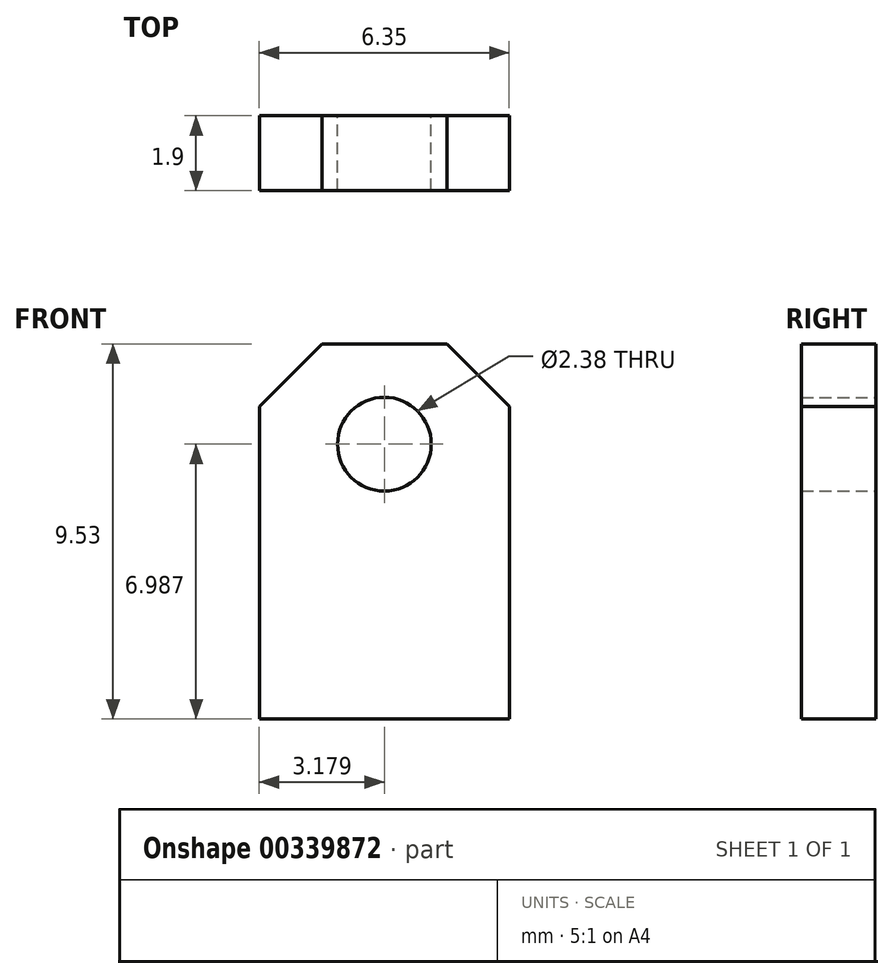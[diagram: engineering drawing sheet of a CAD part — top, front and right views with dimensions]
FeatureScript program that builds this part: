
annotation { "Feature Type Name" : "Feature", "Feature Type Description" : "" }
export const myFeature = defineFeature(function(context is Context, id is Id, definition is map)
    precondition{}
    {
        {
            var Q0;
            Q0=qCreatedBy(makeId("Front.planeOp"),FACE);
            var sketch = newSketch(context, id + "F0", { "sketchPlane" : qUnion([Q0])});
            skLineSegment(sketch, "E0.bottom", {"start": v(-34.55, 25.52) * mm, "end": v(-31.37, 25.52) * mm});
            skLineSegment(sketch, "E0.top", {"start": v(-36.14, 16) * mm, "end": v(-29.79, 16) * mm});
            skLineSegment(sketch, "E0.left", {"start": v(-36.14, 23.93) * mm, "end": v(-36.14, 16) * mm});
            skLineSegment(sketch, "E0.right", {"start": v(-29.79, 23.93) * mm, "end": v(-29.79, 16) * mm});
            skLineSegment(sketch, "E1", {"start": v(-36.14, 23.93) * mm, "end": v(-34.55, 25.52) * mm});
            skLineSegment(sketch, "E2", {"start": v(-31.37, 25.52) * mm, "end": v(-29.79, 23.93) * mm});
            skCircle(sketch, "E3", {"center": v(-32.96, 22.98) * mm, "radius": 1.19 * mm});
            skSolve(sketch);
        }
        {
            var Q0;
            Q0=makeQuery(id+"F0.imprint","IMPRINT",FACE,{"disambiguationData":[TD([[makeQuery(id+"F0.imprint","IMPRINT",EDGE,{"derivedFrom":sQuery(id+"F0.wireOp",EDGE,"E0.bottom")}),-1.0]])]});
            extrude(context, id + "F1", {"entities" : qUnion([Q0]), "depth" : 1.9 * mm});
        }
    });
